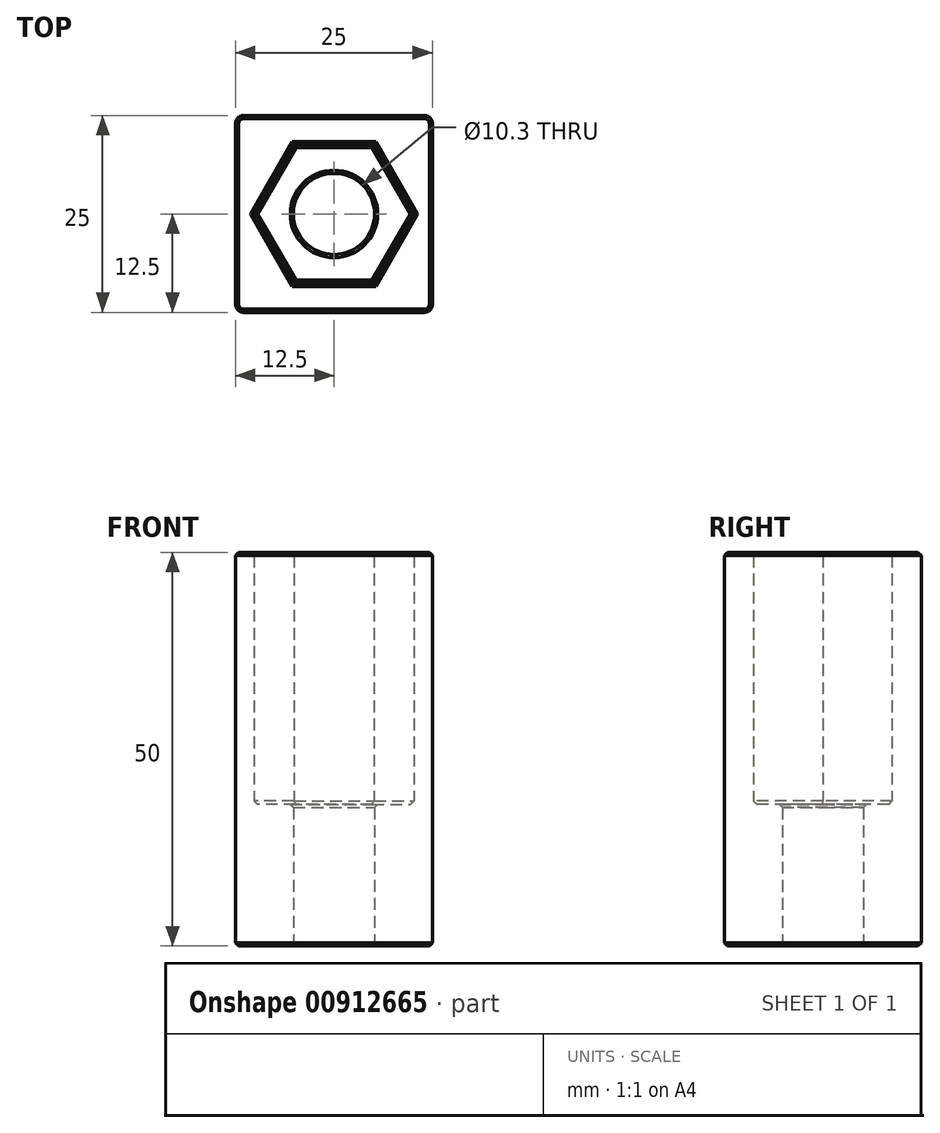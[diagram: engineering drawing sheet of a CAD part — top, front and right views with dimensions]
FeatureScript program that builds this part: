
annotation { "Feature Type Name" : "Feature", "Feature Type Description" : "" }
export const myFeature = defineFeature(function(context is Context, id is Id, definition is map)
    precondition{}
    {
        {
            var Q0;
            Q0=qCreatedBy(makeId("Top.planeOp"),FACE);
            var sketch = newSketch(context, id + "F0", { "sketchPlane" : qUnion([Q0])});
            skLineSegment(sketch, "E0.bottom", {"start": v(-12.5, 12.5) * mm, "end": v(12.5, 12.5) * mm});
            skLineSegment(sketch, "E0.top", {"start": v(-12.5, -12.5) * mm, "end": v(12.5, -12.5) * mm});
            skLineSegment(sketch, "E0.left", {"start": v(-12.5, 12.5) * mm, "end": v(-12.5, -12.5) * mm});
            skLineSegment(sketch, "E0.right", {"start": v(12.5, 12.5) * mm, "end": v(12.5, -12.5) * mm});
            skPoint(sketch, "E0.middle", {"position": v(0, 0) * mm});
            skSolve(sketch);
        }
        {
            var Q0;
            Q0=makeQuery(id+"F0.imprint","IMPRINT",FACE,{"disambiguationData":[TD([[makeQuery(id+"F0.imprint","IMPRINT",EDGE,{"derivedFrom":sQuery(id+"F0.wireOp",EDGE,"E0.bottom")}),-1.0]])]});
            extrude(context, id + "F1", {"entities" : qUnion([Q0]), "depth" : 50 * mm, "offsetDistance" : 25 * mm});
        }
        {
            var Q0;
            Q0=makeQuery(id+"F1.opExtrude","CAP_FACE",FACE,{"disambiguationData":[OSD([sQuery(id+"F0.wireOp",EDGE,"E0.bottom"),sQuery(id+"F0.wireOp",EDGE,"E0.top"),sQuery(id+"F0.wireOp",EDGE,"E0.left"),sQuery(id+"F0.wireOp",EDGE,"E0.right")])],"isStart":false});
            var sketch = newSketch(context, id + "F2", { "sketchPlane" : qUnion([Q0])});
            skCircle(sketch, "E1", {"center": v(0, 0) * mm, "radius": 5.15 * mm});
            skSolve(sketch);
        }
        {
            var Q0;
            Q0=makeQuery(id+"F2.imprint","IMPRINT",FACE,{"disambiguationData":[TD([[makeQuery(id+"F2.imprint","IMPRINT",EDGE,{"derivedFrom":sQuery(id+"F2.wireOp",EDGE,"E1")}),1.0]])]});
            extrude(context, id + "F3", {"entities" : qUnion([Q0]), "operationType" : NewBodyOperationType.REMOVE, "endBound" : BoundingType.THROUGH_ALL, "oppositeDirection" : true, "depth" : 25 * mm, "offsetDistance" : 25 * mm});
        }
        {
            var Q0;
            Q0=makeQuery(id+"F1.opExtrude","CAP_FACE",FACE,{"disambiguationData":[OSD([sQuery(id+"F0.wireOp",EDGE,"E0.bottom"),sQuery(id+"F0.wireOp",EDGE,"E0.top"),sQuery(id+"F0.wireOp",EDGE,"E0.left"),sQuery(id+"F0.wireOp",EDGE,"E0.right")])],"isStart":false});
            var sketch = newSketch(context, id + "F4", { "sketchPlane" : qUnion([Q0])});
            skCircle(sketch, "E2.cCircle", {"center": v(0, 0) * mm, "radius": 8.8 * mm, "construction": true});
            skLineSegment(sketch, "E2.0", {"start": v(-5.08, 8.8) * mm, "end": v(5.08, 8.8) * mm});
            skLineSegment(sketch, "E2.1", {"start": v(5.08, 8.8) * mm, "end": v(10.16, 0) * mm});
            skLineSegment(sketch, "E2.2", {"start": v(10.16, 0) * mm, "end": v(5.08, -8.8) * mm});
            skLineSegment(sketch, "E2.3", {"start": v(5.08, -8.8) * mm, "end": v(-5.08, -8.8) * mm});
            skLineSegment(sketch, "E2.4", {"start": v(-5.08, -8.8) * mm, "end": v(-10.16, 0) * mm});
            skLineSegment(sketch, "E2.5", {"start": v(-10.16, 0) * mm, "end": v(-5.08, 8.8) * mm});
            skPoint(sketch, "E2.0.midPoint", {"position": v(0, 8.8) * mm});
            skSolve(sketch);
        }
        {
            var Q0;
            Q0=makeQuery(id+"F4.imprint","IMPRINT",FACE,{"disambiguationData":[TD([[makeQuery(id+"F4.imprint","IMPRINT",EDGE,{"derivedFrom":sQuery(id+"F4.wireOp",EDGE,"E2.0")}),-1.0]])]});
            extrude(context, id + "F5", {"entities" : qUnion([Q0]), "operationType" : NewBodyOperationType.REMOVE, "endBound" : BoundingType.THROUGH_ALL, "oppositeDirection" : true, "depth" : 25 * mm, "offsetDistance" : 25 * mm, "hasSecondDirection" : true, "secondDirectionOppositeDirection" : false, "secondDirectionDepth" : -18 * mm});
        }
        {
            var Q0;
            Q0=makeQuery(id+"F1.opExtrude","SWEPT_EDGE",EDGE,{"disambiguationData":[OSD([sQuery(id+"F0.wireOp",EDGE,"E0.bottom"),sQuery(id+"F0.wireOp",EDGE,"E0.left")])]});
            var Q1;
            Q1=makeQuery(id+"F1.opExtrude","SWEPT_EDGE",EDGE,{"disambiguationData":[OSD([sQuery(id+"F0.wireOp",EDGE,"E0.top"),sQuery(id+"F0.wireOp",EDGE,"E0.left")])]});
            var Q2;
            Q2=makeQuery(id+"F1.opExtrude","SWEPT_EDGE",EDGE,{"disambiguationData":[OSD([sQuery(id+"F0.wireOp",EDGE,"E0.bottom"),sQuery(id+"F0.wireOp",EDGE,"E0.right")])]});
            var Q3;
            Q3=makeQuery(id+"F1.opExtrude","SWEPT_EDGE",EDGE,{"disambiguationData":[OSD([sQuery(id+"F0.wireOp",EDGE,"E0.top"),sQuery(id+"F0.wireOp",EDGE,"E0.right")])]});
            fillet(context, id + "F6", {"entities" : qUnion([Q0, Q1, Q2, Q3]), "radius" : 1 * mm, "tangentPropagation" : true, "allowEdgeOverflow" : false});
        }
        {
            var Q0;
            Q0=makeQuery(id+"F1.opExtrude","CAP_FACE",FACE,{"disambiguationData":[OSD([sQuery(id+"F0.wireOp",EDGE,"E0.bottom"),sQuery(id+"F0.wireOp",EDGE,"E0.top"),sQuery(id+"F0.wireOp",EDGE,"E0.left"),sQuery(id+"F0.wireOp",EDGE,"E0.right")])],"isStart":true});
            var Q1;
            Q1=makeQuery(id+"F1.opExtrude","CAP_FACE",FACE,{"disambiguationData":[OSD([sQuery(id+"F0.wireOp",EDGE,"E0.bottom"),sQuery(id+"F0.wireOp",EDGE,"E0.top"),sQuery(id+"F0.wireOp",EDGE,"E0.left"),sQuery(id+"F0.wireOp",EDGE,"E0.right")])],"isStart":false});
            var Q2;
            Q2=makeQuery(id+"F5.boolean.opBoolean","COPY",FACE,{"derivedFrom":makeQuery(id+"F5.opExtrude","CAP_FACE",FACE,{"disambiguationData":[OSD([sQuery(id+"F2.wireOp",EDGE,"E1"),sQuery(id+"F4.wireOp",EDGE,"E2.0"),sQuery(id+"F4.wireOp",EDGE,"E2.1"),sQuery(id+"F4.wireOp",EDGE,"E2.2"),sQuery(id+"F4.wireOp",EDGE,"E2.3"),sQuery(id+"F4.wireOp",EDGE,"E2.4"),sQuery(id+"F4.wireOp",EDGE,"E2.5")])],"isStart":true})});
            chamfer(context, id + "F7", {"entities" : qUnion([Q0, Q1, Q2]), "width" : 0.4 * mm, "tangentPropagation" : true});
        }
        {
            var Q0;
            Q0=makeQuery(id+"F1.opExtrude","SWEPT_BODY",BODY,{"disambiguationData":[OSD([sQuery(id+"F0.wireOp",EDGE,"E0.bottom"),sQuery(id+"F0.wireOp",EDGE,"E0.top"),sQuery(id+"F0.wireOp",EDGE,"E0.left"),sQuery(id+"F0.wireOp",EDGE,"E0.right")])]});
            var Q1;
            {var subQ0=sQuery(id+"F0.wireOp",EDGE,"E0.right");Q1=makeQuery(id+"F7.opChamfer","BLEND_EDGE",EDGE,{"blendedFrom":[makeQuery(id+"F1.opExtrude","CAP_EDGE",EDGE,{"disambiguationData":[OSD([subQ0])],"isStart":false}),makeQuery(id+"F1.opExtrude","CAP_FACE",FACE,{"disambiguationData":[OSD([sQuery(id+"F0.wireOp",EDGE,"E0.bottom"),sQuery(id+"F0.wireOp",EDGE,"E0.top"),sQuery(id+"F0.wireOp",EDGE,"E0.left"),subQ0])],"isStart":false})],"blendedInto":[makeQuery(id+"F1.opExtrude","CAP_FACE",FACE,{"disambiguationData":[OSD([sQuery(id+"F0.wireOp",EDGE,"E0.bottom"),sQuery(id+"F0.wireOp",EDGE,"E0.top"),sQuery(id+"F0.wireOp",EDGE,"E0.left"),subQ0])],"isStart":false})]});}
            transform(context, id + "F8", {"entities" : qUnion([Q0]), "transformType" : TransformType.ROTATION, "transformAxis" : qUnion([Q1]), "angle" : 180 * degree, "makeCopy" : false});
        }
    });
